# Revit family: Domotics-DomesticRanges-GEWISS-27COMBI_SYSTEM-IP40_BUZZER
name_source: partatom
category: Modelli generici
revit_build: Autodesk Revit 2016 (Build: 20161004_0715(x64)
units: mm (PartAtom-declared; Revit-internal decimal feet)

## family parameters
Condiviso = No
Host = Superficie
Punto di calcolo locali = No
Può ospitare armatura = No
Quota connettore circolare = Usa diametro
Taglio con vuoti quando caricato = No
Tipo di parte = Normale

## types (2) — shared parameters
Altezza = 800 mm  [stored 2.62467 ft]
Catalogue = DOMOTICS
Catalogue Range = 27COMBI
Colour = Grey RAL 7035
Electrocod = 0132
Frequency impulses of sound = 1HZ
Glow Wire Test = 650°C
IDF = f5ea6f11-fb25-4f0e-85b2-17e66f9e58b0
IDT = 42373ce3-cb7a-4058-9c9c-5d702b03e44c
IP degree = IP40
Immagine tipo = GW26427.jpg
Installation temperature = -25 +60 °C
Insulation class = II
Larghezza = 640 mm
Outer dim. LxHxD (mm) = 64x80x59
Produttore = GEWISS S.p.A.
Profonfità = 590 mm  [stored 1.9357 ft]
Prospetto di default = 1219 mm
Sound intensity = 70 dB (at 1 m)
Standard = EN 62080
Technical sheet = https://www.gewiss.com
Thermo-pressure with ball = 70
URL = https://www.gewiss.com
Version file RFA = 18.0

## per-type parameters (varying)
| type | Descrizione | EAN code | Modello | Rated voltage |
| GW26427 - 230V acoustic alarm | 230V ACOUSTIC ALARM | 8011564033238 | GW26427 | 230V ac |
| GW26417 - 24V acoustic alarm | 24V ACOUSTIC ALARM | 8011564033207 | GW26417 | 24 V ac |

note: source unit labels omitted for Thermo-pressure with ball — the stored unit's dimension contradicts the parameter name (converter mislabeling)

note: [stored X ft] marks values corroborated as IEEE doubles in the binary element streams (Revit-internal decimal feet)
